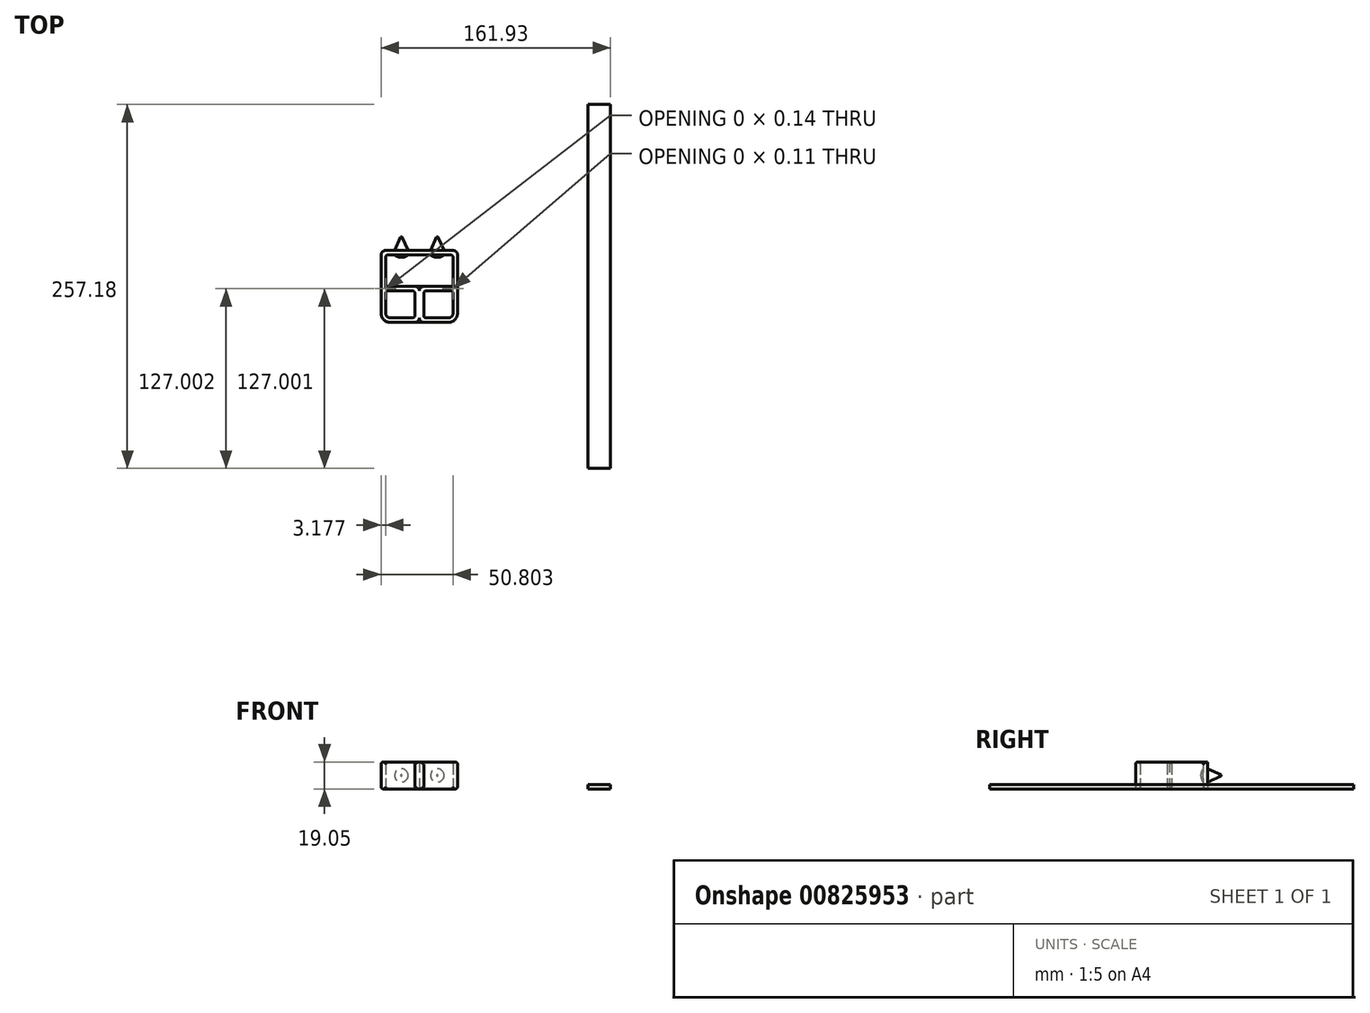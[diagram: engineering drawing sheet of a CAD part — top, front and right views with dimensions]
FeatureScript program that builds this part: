
annotation { "Feature Type Name" : "Feature", "Feature Type Description" : "" }
export const myFeature = defineFeature(function(context is Context, id is Id, definition is map)
    precondition{}
    {
        {
            var Q0;
            Q0=qCreatedBy(makeId("Top.planeOp"),FACE);
            var sketch = newSketch(context, id + "F0", { "sketchPlane" : qUnion([Q0])});
            skLineSegment(sketch, "E0.bottom", {"start": v(20.64, -22.23) * mm, "end": v(4.76, -22.23) * mm});
            skLineSegment(sketch, "E0.top", {"start": v(22.22, 22.23) * mm, "end": v(-22.23, 22.23) * mm});
            skLineSegment(sketch, "E0.left", {"start": v(23.81, -19.05) * mm, "end": v(23.81, 20.64) * mm});
            skLineSegment(sketch, "E0.right", {"start": v(-23.81, -19.05) * mm, "end": v(-23.81, 20.64) * mm});
            skPoint(sketch, "E0.middle", {"position": v(0, 0) * mm});
            skLineSegment(sketch, "E1.bottom", {"start": v(-3.17, -25.4) * mm, "end": v(-20.64, -25.4) * mm});
            skLineSegment(sketch, "E1.top", {"start": v(23.81, 25.4) * mm, "end": v(-23.81, 25.4) * mm});
            skLineSegment(sketch, "E1.left", {"start": v(26.99, -19.05) * mm, "end": v(26.99, 22.23) * mm});
            skLineSegment(sketch, "E1.right", {"start": v(-26.99, -19.05) * mm, "end": v(-26.99, 22.23) * mm});
            skLineSegment(sketch, "E2", {"start": v(0, -3.18) * mm, "end": v(0, -22.22) * mm});
            skLineSegment(sketch, "E3", {"start": v(3.18, 0) * mm, "end": v(23.81, 0) * mm});
            skLineSegment(sketch, "E4", {"start": v(-23.81, -3.18) * mm, "end": v(-4.76, -3.18) * mm});
            skLineSegment(sketch, "E5", {"start": v(3.18, -4.76) * mm, "end": v(3.18, -20.64) * mm});
            skLineSegment(sketch, "E6", {"start": v(-3.17, -4.76) * mm, "end": v(-3.17, -20.64) * mm});
            skPoint(sketch, "E7.orphan", {"position": v(-26.99, 0) * mm});
            skLineSegment(sketch, "E8.trimOffspring", {"start": v(4.76, -3.18) * mm, "end": v(23.81, -3.18) * mm});
            skLineSegment(sketch, "E9.trimOffspring", {"start": v(-4.76, -22.23) * mm, "end": v(-20.64, -22.23) * mm});
            skPoint(sketch, "E10.orphan", {"position": v(26.99, 0) * mm});
            skArc(sketch, "E11.filletArc", {"start": v(3.18, 0) * mm, "mid": v(0.93, -0.93) * mm, "end": v(0, -3.18) * mm});
            skLineSegment(sketch, "E12", {"start": v(-23.81, 0) * mm, "end": v(-3.18, 0) * mm});
            skLineSegment(sketch, "E13", {"start": v(0, -3.17) * mm, "end": v(0, -3.18) * mm});
            skArc(sketch, "E14.filletArc", {"start": v(0, -3.17) * mm, "mid": v(-0.93, -0.93) * mm, "end": v(-3.18, 0) * mm});
            skArc(sketch, "E15.filletArc", {"start": v(4.76, -3.18) * mm, "mid": v(3.64, -3.64) * mm, "end": v(3.18, -4.76) * mm});
            skPoint(sketch, "E16.visualSharp", {"position": v(-3.17, -3.18) * mm});
            skArc(sketch, "E16.filletArc", {"start": v(-3.17, -4.76) * mm, "mid": v(-3.64, -3.64) * mm, "end": v(-4.76, -3.18) * mm});
            skPoint(sketch, "E17.newPointA", {"position": v(26.99, -25.4) * mm});
            skPoint(sketch, "E17.newPointB", {"position": v(0, -25.4) * mm});
            skArc(sketch, "E17.filletArc", {"start": v(-3.18, -25.4) * mm, "mid": v(-0.93, -24.47) * mm, "end": v(0, -22.22) * mm});
            skLineSegment(sketch, "E18", {"start": v(3.18, -25.4) * mm, "end": v(20.64, -25.4) * mm});
            skLineSegment(sketch, "E19", {"start": v(0, -22.22) * mm, "end": v(0, -22.22) * mm});
            skArc(sketch, "E20.filletArc", {"start": v(0, -22.22) * mm, "mid": v(0.93, -24.47) * mm, "end": v(3.18, -25.4) * mm});
            skPoint(sketch, "E21.visualSharp", {"position": v(3.18, -22.23) * mm});
            skArc(sketch, "E21.filletArc", {"start": v(3.18, -20.64) * mm, "mid": v(3.64, -21.76) * mm, "end": v(4.76, -22.23) * mm});
            skPoint(sketch, "E22.visualSharp", {"position": v(-3.17, -22.23) * mm});
            skArc(sketch, "E22.filletArc", {"start": v(-4.76, -22.23) * mm, "mid": v(-3.64, -21.76) * mm, "end": v(-3.17, -20.64) * mm});
            skPoint(sketch, "E23.visualSharp", {"position": v(-26.99, -25.4) * mm});
            skArc(sketch, "E23.filletArc", {"start": v(-26.99, -19.05) * mm, "mid": v(-25.13, -23.54) * mm, "end": v(-20.64, -25.4) * mm});
            skPoint(sketch, "E24.visualSharp", {"position": v(-23.81, -22.23) * mm});
            skArc(sketch, "E24.filletArc", {"start": v(-23.81, -19.05) * mm, "mid": v(-22.88, -21.3) * mm, "end": v(-20.64, -22.23) * mm});
            skArc(sketch, "E25.filletArc", {"start": v(20.64, -25.4) * mm, "mid": v(25.13, -23.54) * mm, "end": v(26.99, -19.05) * mm});
            skPoint(sketch, "E26.visualSharp", {"position": v(23.81, -22.23) * mm});
            skArc(sketch, "E26.filletArc", {"start": v(20.64, -22.23) * mm, "mid": v(22.88, -21.3) * mm, "end": v(23.81, -19.05) * mm});
            skPoint(sketch, "E27.visualSharp", {"position": v(23.81, 22.23) * mm});
            skArc(sketch, "E27.filletArc", {"start": v(23.81, 20.64) * mm, "mid": v(23.35, 21.76) * mm, "end": v(22.22, 22.23) * mm});
            skPoint(sketch, "E28.visualSharp", {"position": v(26.99, 25.4) * mm});
            skArc(sketch, "E28.filletArc", {"start": v(26.99, 22.23) * mm, "mid": v(26.06, 24.47) * mm, "end": v(23.81, 25.4) * mm});
            skPoint(sketch, "E29.visualSharp", {"position": v(-26.99, 25.4) * mm});
            skArc(sketch, "E29.filletArc", {"start": v(-23.81, 25.4) * mm, "mid": v(-26.06, 24.47) * mm, "end": v(-26.99, 22.23) * mm});
            skArc(sketch, "E30.filletArc", {"start": v(-22.23, 22.23) * mm, "mid": v(-23.35, 21.76) * mm, "end": v(-23.81, 20.64) * mm});
            skLineSegment(sketch, "E31", {"start": v(-23.81, -1.59) * mm, "end": v(-23.81, -1.59) * mm});
            skPoint(sketch, "E32.visualSharp", {"position": v(-23.81, 0) * mm});
            skPoint(sketch, "E33.visualSharp", {"position": v(-23.81, -3.18) * mm});
            skLineSegment(sketch, "E34", {"start": v(23.81, -1.59) * mm, "end": v(23.81, -1.59) * mm});
            skPoint(sketch, "E35.visualSharp", {"position": v(23.81, 0) * mm});
            skPoint(sketch, "E36.visualSharp", {"position": v(23.81, -3.18) * mm});
            skArc(sketch, "E37", {"start": v(22.22, 0) * mm, "mid": v(23.81, -1.55) * mm, "end": v(22.3, -3.18) * mm});
            skArc(sketch, "E38", {"start": v(-22.23, 0) * mm, "mid": v(-23.81, -1.64) * mm, "end": v(-22.13, -3.18) * mm});
            skLineSegment(sketch, "E39", {"start": v(-3.18, 0) * mm, "end": v(3.18, 0) * mm});
            skLineSegment(sketch, "E40", {"start": v(-3.17, -25.4) * mm, "end": v(3.18, -25.4) * mm});
            skSolve(sketch);
        }
        {
            var Q0;
            Q0=makeQuery(id+"F0.imprint","IMPRINT",FACE,{"disambiguationData":[TD([[makeQuery(id+"F0.imprint","IMPRINT",EDGE,{"derivedFrom":sQuery(id+"F0.wireOp",EDGE,"E0.bottom")}),1.0]])]});
            var Q1;
            {var subQ0=sQuery(id+"F0.wireOp",EDGE,"E4");var subQ1=sQuery(id+"F0.wireOp",EDGE,"E0.right");var subQ2=makeQuery(id+"F0.imprint","INTERSECT",VERTEX,{"derivedFrom":[subQ1,subQ0]});Q1=makeQuery(id+"F0.imprint","IMPRINT",FACE,{"disambiguationData":[TD([[makeQuery(id+"F0.imprint","IMPRINT",EDGE,{"disambiguationData":[TD([[subQ2,-1.0]])],"derivedFrom":subQ1}),-1.0]])]});}
            var Q2;
            {var subQ0=sQuery(id+"F0.wireOp",EDGE,"E12");var subQ1=sQuery(id+"F0.wireOp",EDGE,"E0.right");var subQ2=makeQuery(id+"F0.imprint","INTERSECT",VERTEX,{"derivedFrom":[subQ1,subQ0]});Q2=makeQuery(id+"F0.imprint","IMPRINT",FACE,{"disambiguationData":[TD([[makeQuery(id+"F0.imprint","IMPRINT",EDGE,{"disambiguationData":[TD([[subQ2,1.0]])],"derivedFrom":subQ1}),-1.0]])]});}
            var Q3;
            {var subQ0=sQuery(id+"F0.wireOp",EDGE,"E8.trimOffspring");var subQ1=sQuery(id+"F0.wireOp",EDGE,"E0.left");var subQ2=makeQuery(id+"F0.imprint","INTERSECT",VERTEX,{"derivedFrom":[subQ1,subQ0]});Q3=makeQuery(id+"F0.imprint","IMPRINT",FACE,{"disambiguationData":[TD([[makeQuery(id+"F0.imprint","IMPRINT",EDGE,{"disambiguationData":[TD([[subQ2,-1.0]])],"derivedFrom":subQ1}),1.0]])]});}
            var Q4;
            {var subQ0=sQuery(id+"F0.wireOp",EDGE,"E3");var subQ1=sQuery(id+"F0.wireOp",EDGE,"E0.left");var subQ2=makeQuery(id+"F0.imprint","INTERSECT",VERTEX,{"derivedFrom":[subQ1,subQ0]});Q4=makeQuery(id+"F0.imprint","IMPRINT",FACE,{"disambiguationData":[TD([[makeQuery(id+"F0.imprint","IMPRINT",EDGE,{"disambiguationData":[TD([[subQ2,1.0]])],"derivedFrom":subQ1}),1.0]])]});}
            extrude(context, id + "F1", {"entities" : qUnion([Q0, Q1, Q2, Q3, Q4]), "depth" : 19.05 * mm, "offsetDistance" : 25.4 * mm});
        }
        {
            var Q0;
            Q0=makeQuery(id+"F0.imprint","IMPRINT",FACE,{"disambiguationData":[TD([[makeQuery(id+"F0.imprint","IMPRINT",EDGE,{"derivedFrom":sQuery(id+"F0.wireOp",EDGE,"E11.filletArc")}),-1.0]])]});
            var Q1;
            Q1=makeQuery(id+"F0.imprint","IMPRINT",FACE,{"disambiguationData":[TD([[makeQuery(id+"F0.imprint","IMPRINT",EDGE,{"derivedFrom":sQuery(id+"F0.wireOp",EDGE,"E17.filletArc")}),-1.0]])]});
            extrude(context, id + "F2", {"entities" : qUnion([Q0, Q1]), "depth" : 19.05 * mm, "offsetDistance" : 25.4 * mm});
        }
        {
            var Q0;
            Q0=makeQuery(id+"F1.opExtrude","SWEPT_FACE",FACE,{"disambiguationData":[OSD([sQuery(id+"F0.wireOp",EDGE,"E18")])]});
            var Q1;
            Q1=makeQuery(id+"F1.opExtrude","SWEPT_FACE",FACE,{"disambiguationData":[OSD([sQuery(id+"F0.wireOp",EDGE,"E1.bottom")])]});
            var Q2;
            Q2=makeQuery(id+"F2.opExtrude","CAP_EDGE",EDGE,{"disambiguationData":[OSD([sQuery(id+"F0.wireOp",EDGE,"E40")])],"isStart":false});
            var Q3;
            Q3=makeQuery(id+"F2.opExtrude","CAP_EDGE",EDGE,{"disambiguationData":[OSD([sQuery(id+"F0.wireOp",EDGE,"E40")])],"isStart":true});
            var Q4;
            Q4=makeQuery(id+"F1.opExtrude","SWEPT_FACE",FACE,{"disambiguationData":[OSD([sQuery(id+"F0.wireOp",EDGE,"E1.right")])]});
            var Q5;
            Q5=makeQuery(id+"F1.opExtrude","SWEPT_FACE",FACE,{"disambiguationData":[OSD([sQuery(id+"F0.wireOp",EDGE,"E23.filletArc")])]});
            var Q6;
            Q6=makeQuery(id+"F1.opExtrude","SWEPT_FACE",FACE,{"disambiguationData":[OSD([sQuery(id+"F0.wireOp",EDGE,"E1.left")])]});
            var Q7;
            Q7=makeQuery(id+"F1.opExtrude","SWEPT_FACE",FACE,{"disambiguationData":[OSD([sQuery(id+"F0.wireOp",EDGE,"E25.filletArc")])]});
            var Q8;
            Q8=makeQuery(id+"F1.opExtrude","SWEPT_FACE",FACE,{"disambiguationData":[OSD([sQuery(id+"F0.wireOp",EDGE,"E5")])]});
            var Q9;
            Q9=makeQuery(id+"F1.opExtrude","SWEPT_FACE",FACE,{"disambiguationData":[OSD([sQuery(id+"F0.wireOp",EDGE,"E8.trimOffspring")])]});
            var Q10;
            Q10=makeQuery(id+"F1.opExtrude","SWEPT_FACE",FACE,{"disambiguationData":[OSD([sQuery(id+"F0.wireOp",EDGE,"E15.filletArc")])]});
            var Q11;
            Q11=makeQuery(id+"F1.opExtrude","SWEPT_FACE",FACE,{"disambiguationData":[OSD([sQuery(id+"F0.wireOp",EDGE,"E0.bottom")])]});
            var Q12;
            {var subQ0=sQuery(id+"F0.wireOp",EDGE,"E0.left");Q12=makeQuery(id+"F1.opExtrude","SWEPT_FACE",FACE,{"disambiguationData":[OSD([subQ0]),TDD([makeQuery(id+"F0.imprint","IMPRINT",EDGE,{"disambiguationData":[TD([[makeQuery(id+"F0.imprint","INTERSECT",VERTEX,{"derivedFrom":[subQ0,sQuery(id+"F0.wireOp",EDGE,"E26.filletArc")]}),-1.0]])],"derivedFrom":subQ0})])]});}
            var Q13;
            Q13=makeQuery(id+"F1.opExtrude","SWEPT_FACE",FACE,{"disambiguationData":[OSD([sQuery(id+"F0.wireOp",EDGE,"E26.filletArc")])]});
            var Q14;
            Q14=makeQuery(id+"F1.opExtrude","SWEPT_FACE",FACE,{"disambiguationData":[OSD([sQuery(id+"F0.wireOp",EDGE,"E21.filletArc")])]});
            var Q15;
            Q15=makeQuery(id+"F1.opExtrude","SWEPT_FACE",FACE,{"disambiguationData":[OSD([sQuery(id+"F0.wireOp",EDGE,"E9.trimOffspring")])]});
            var Q16;
            Q16=makeQuery(id+"F1.opExtrude","SWEPT_FACE",FACE,{"disambiguationData":[OSD([sQuery(id+"F0.wireOp",EDGE,"E22.filletArc")])]});
            var Q17;
            Q17=makeQuery(id+"F1.opExtrude","SWEPT_FACE",FACE,{"disambiguationData":[OSD([sQuery(id+"F0.wireOp",EDGE,"E6")])]});
            var Q18;
            Q18=makeQuery(id+"F1.opExtrude","SWEPT_FACE",FACE,{"disambiguationData":[OSD([sQuery(id+"F0.wireOp",EDGE,"E24.filletArc")])]});
            var Q19;
            {var subQ0=sQuery(id+"F0.wireOp",EDGE,"E0.right");Q19=makeQuery(id+"F1.opExtrude","SWEPT_FACE",FACE,{"disambiguationData":[OSD([subQ0]),TDD([makeQuery(id+"F0.imprint","IMPRINT",EDGE,{"disambiguationData":[TD([[makeQuery(id+"F0.imprint","INTERSECT",VERTEX,{"derivedFrom":[subQ0,sQuery(id+"F0.wireOp",EDGE,"E24.filletArc")]}),-1.0]])],"derivedFrom":subQ0})])]});}
            var Q20;
            Q20=makeQuery(id+"F1.opExtrude","SWEPT_FACE",FACE,{"disambiguationData":[OSD([sQuery(id+"F0.wireOp",EDGE,"E16.filletArc")])]});
            var Q21;
            Q21=makeQuery(id+"F1.opExtrude","SWEPT_FACE",FACE,{"disambiguationData":[OSD([sQuery(id+"F0.wireOp",EDGE,"E4")])]});
            fillet(context, id + "F3", {"entities" : qUnion([Q0, Q1, Q2, Q3, Q4, Q5, Q6, Q7, Q8, Q9, Q10, Q11, Q12, Q13, Q14, Q15, Q16, Q17, Q18, Q19, Q20, Q21]), "radius" : 1.59 * mm, "allowEdgeOverflow" : false});
        }
        {
            var Q0;
            Q0=qCreatedBy(makeId("Right.planeOp"),FACE);
            var sketch = newSketch(context, id + "F4", { "sketchPlane" : qUnion([Q0])});
            skLineSegment(sketch, "E41", {"start": v(-3.18, 0) * mm, "end": v(-3.18, 19.05) * mm, "construction": true});
            skArc(sketch, "E42", {"start": v(0, 17.46) * mm, "mid": v(-0.46, 18.59) * mm, "end": v(-1.59, 19.05) * mm});
            skArc(sketch, "E43", {"start": v(-1.59, 0) * mm, "mid": v(-0.46, 0.46) * mm, "end": v(0, 1.59) * mm});
            skLineSegment(sketch, "E44", {"start": v(-1.59, 0) * mm, "end": v(0, 0) * mm});
            skLineSegment(sketch, "E45", {"start": v(0, 0) * mm, "end": v(0, 1.59) * mm});
            skLineSegment(sketch, "E46", {"start": v(-1.59, 19.05) * mm, "end": v(0, 19.05) * mm});
            skLineSegment(sketch, "E47", {"start": v(0, 19.05) * mm, "end": v(0, 17.46) * mm});
            skSolve(sketch);
        }
        {
            var Q0;
            Q0 = qSketchRegion(id + "F4", true);
            extrude(context, id + "F5", {"entities" : qUnion([Q0]), "operationType" : NewBodyOperationType.REMOVE, "oppositeDirection" : true, "depth" : 23.8 * mm, "offsetDistance" : 25.4 * mm, "hasSecondDirection" : true, "secondDirectionOppositeDirection" : false, "secondDirectionDepth" : 23.8 * mm});
        }
        {
            var Q0;
            Q0=qCreatedBy(makeId("Front.planeOp"),FACE);
            var sketch = newSketch(context, id + "F6", { "sketchPlane" : qUnion([Q0])});
            skCircle(sketch, "E48", {"center": v(-12.7, 9.53) * mm, "radius": 4.76 * mm});
            skCircle(sketch, "E49", {"center": v(12.7, 9.53) * mm, "radius": 4.76 * mm});
            skSolve(sketch);
        }
        {
            var Q0;
            Q0 = qSketchRegion(id + "F6", true);
            extrude(context, id + "F7", {"entities" : qUnion([Q0]), "operationType" : NewBodyOperationType.ADD, "oppositeDirection" : true, "depth" : 34.92 * mm, "offsetDistance" : 25.4 * mm, "hasSecondDirection" : true, "secondDirectionOppositeDirection" : true, "secondDirectionDepth" : 20.64 * mm});
        }
        {
            var Q0;
            Q0=makeQuery(id+"F7.opExtrude","CAP_FACE",FACE,{"disambiguationData":[OSD([sQuery(id+"F6.wireOp",EDGE,"E49")])],"isStart":false});
            var Q1;
            Q1=makeQuery(id+"F7.opExtrude","CAP_FACE",FACE,{"disambiguationData":[OSD([sQuery(id+"F6.wireOp",EDGE,"E48")])],"isStart":false});
            chamfer(context, id + "F8", {"entities" : qUnion([Q0, Q1]), "chamferType" : ChamferType.TWO_OFFSETS, "width1" : 9.52 * mm, "oppositeDirection" : false, "width2" : 4.32 * mm, "tangentPropagation" : true});
        }
        {
            var Q0;
            Q0=makeQuery(id+"F7.opExtrude","CAP_FACE",FACE,{"disambiguationData":[OSD([sQuery(id+"F6.wireOp",EDGE,"E48")])],"isStart":true});
            var Q1;
            Q1=makeQuery(id+"F7.opExtrude","CAP_FACE",FACE,{"disambiguationData":[OSD([sQuery(id+"F6.wireOp",EDGE,"E49")])],"isStart":true});
            fillet(context, id + "F9", {"entities" : qUnion([Q0, Q1]), "radius" : 6.35 * mm, "tangentPropagation" : true, "allowEdgeOverflow" : false});
        }
        {
            var Q0;
            Q0=qCreatedBy(makeId("Top.planeOp"),FACE);
            var sketch = newSketch(context, id + "F10", { "sketchPlane" : qUnion([Q0])});
            skLineSegment(sketch, "E50.bottom", {"start": v(134.94, -128.59) * mm, "end": v(119.06, -128.59) * mm});
            skLineSegment(sketch, "E50.top", {"start": v(134.94, 128.59) * mm, "end": v(119.06, 128.59) * mm});
            skLineSegment(sketch, "E50.left", {"start": v(134.94, -128.59) * mm, "end": v(134.94, 128.59) * mm});
            skLineSegment(sketch, "E50.right", {"start": v(119.06, -128.59) * mm, "end": v(119.06, 128.59) * mm});
            skPoint(sketch, "E50.middle", {"position": v(127, 0) * mm});
            skLineSegment(sketch, "E51", {"start": v(119.06, 88.9) * mm, "end": v(134.94, 88.9) * mm});
            skLineSegment(sketch, "E52", {"start": v(119.06, 68.26) * mm, "end": v(134.94, 68.26) * mm});
            skLineSegment(sketch, "E53", {"start": v(119.06, 23.81) * mm, "end": v(134.94, 23.81) * mm});
            skLineSegment(sketch, "E54", {"start": v(119.06, -23.81) * mm, "end": v(134.94, -23.81) * mm});
            skLineSegment(sketch, "E55", {"start": v(119.06, -68.26) * mm, "end": v(134.94, -68.26) * mm});
            skLineSegment(sketch, "E56", {"start": v(119.06, -88.9) * mm, "end": v(134.94, -88.9) * mm});
            skLineSegment(sketch, "E57", {"start": v(119.06, -107.95) * mm, "end": v(134.94, -107.95) * mm});
            skLineSegment(sketch, "E58", {"start": v(119.06, 107.95) * mm, "end": v(134.94, 107.95) * mm});
            skSolve(sketch);
        }
        {
            var Q0;
            {var subQ0=sQuery(id+"F10.wireOp",EDGE,"E56");Q0=makeQuery(id+"F10.imprint","IMPRINT",FACE,{"disambiguationData":[TD([[makeQuery(id+"F10.imprint","IMPRINT",EDGE,{"derivedFrom":subQ0}),-1.0]])]});}
            var Q1;
            {var subQ0=sQuery(id+"F10.wireOp",EDGE,"E55");Q1=makeQuery(id+"F10.imprint","IMPRINT",FACE,{"disambiguationData":[TD([[makeQuery(id+"F10.imprint","IMPRINT",EDGE,{"derivedFrom":subQ0}),-1.0]])]});}
            var Q2;
            {var subQ0=sQuery(id+"F10.wireOp",EDGE,"E54");Q2=makeQuery(id+"F10.imprint","IMPRINT",FACE,{"disambiguationData":[TD([[makeQuery(id+"F10.imprint","IMPRINT",EDGE,{"derivedFrom":subQ0}),-1.0]])]});}
            var Q3;
            {var subQ0=sQuery(id+"F10.wireOp",EDGE,"E53");Q3=makeQuery(id+"F10.imprint","IMPRINT",FACE,{"disambiguationData":[TD([[makeQuery(id+"F10.imprint","IMPRINT",EDGE,{"derivedFrom":subQ0}),-1.0]])]});}
            var Q4;
            {var subQ0=sQuery(id+"F10.wireOp",EDGE,"E52");Q4=makeQuery(id+"F10.imprint","IMPRINT",FACE,{"disambiguationData":[TD([[makeQuery(id+"F10.imprint","IMPRINT",EDGE,{"derivedFrom":subQ0}),-1.0]])]});}
            var Q5;
            {var subQ0=sQuery(id+"F10.wireOp",EDGE,"E51");Q5=makeQuery(id+"F10.imprint","IMPRINT",FACE,{"disambiguationData":[TD([[makeQuery(id+"F10.imprint","IMPRINT",EDGE,{"derivedFrom":subQ0}),-1.0]])]});}
            var Q6;
            {var subQ0=sQuery(id+"F10.wireOp",EDGE,"E51");Q6=makeQuery(id+"F10.imprint","IMPRINT",FACE,{"disambiguationData":[TD([[makeQuery(id+"F10.imprint","IMPRINT",EDGE,{"derivedFrom":subQ0}),1.0]])]});}
            var Q7;
            {var subQ0=sQuery(id+"F10.wireOp",EDGE,"E50.bottom");Q7=makeQuery(id+"F10.imprint","IMPRINT",FACE,{"disambiguationData":[TD([[makeQuery(id+"F10.imprint","IMPRINT",EDGE,{"derivedFrom":subQ0}),-1.0]])]});}
            var Q8;
            {var subQ0=sQuery(id+"F10.wireOp",EDGE,"E50.top");Q8=makeQuery(id+"F10.imprint","IMPRINT",FACE,{"disambiguationData":[TD([[makeQuery(id+"F10.imprint","IMPRINT",EDGE,{"derivedFrom":subQ0}),1.0]])]});}
            extrude(context, id + "F11", {"entities" : qUnion([Q0, Q1, Q2, Q3, Q4, Q5, Q6, Q7, Q8]), "depth" : 3.17 * mm, "offsetDistance" : 25.4 * mm});
        }
        {
            var Q0;
            Q0=sQuery(id+"F10.wireOp",EDGE,"E52");
            var Q1;
            Q1=sQuery(id+"F10.wireOp",EDGE,"E55");
            var Q2;
            Q2=sQuery(id+"F10.wireOp",EDGE,"E56");
            var Q3;
            Q3=sQuery(id+"F10.wireOp",EDGE,"E51");
            var Q4;
            Q4=sQuery(id+"F10.wireOp",EDGE,"E58");
            var Q5;
            Q5=sQuery(id+"F10.wireOp",EDGE,"E57");
            var Q6;
            Q6=sQuery(id+"F10.wireOp",EDGE,"E54");
            var Q7;
            Q7=sQuery(id+"F10.wireOp",EDGE,"E53");
            extrude(context, id + "F12", {"bodyType" : ToolBodyType.SURFACE, "surfaceEntities" : qUnion([Q0, Q1, Q2, Q3, Q4, Q5, Q6, Q7]), "depth" : 3.17 * mm, "offsetDistance" : 25.4 * mm});
        }
    });
